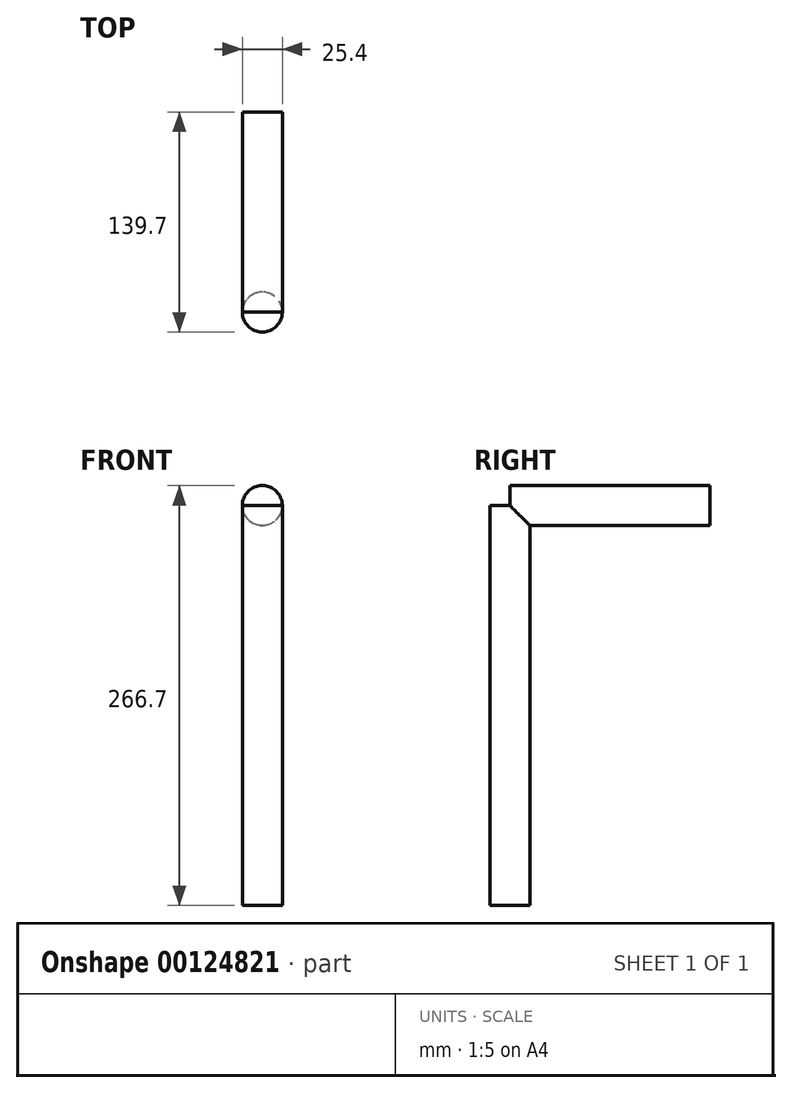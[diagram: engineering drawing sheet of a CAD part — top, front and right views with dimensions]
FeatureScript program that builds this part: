
annotation { "Feature Type Name" : "Feature", "Feature Type Description" : "" }
export const myFeature = defineFeature(function(context is Context, id is Id, definition is map)
    precondition{}
    {
        {
            var Q0;
            Q0=qCreatedBy(makeId("Top.planeOp"),FACE);
            var sketch = newSketch(context, id + "F0", { "sketchPlane" : qUnion([Q0])});
            skCircle(sketch, "E0", {"center": v(0, 0) * mm, "radius": 12.7 * mm});
            skSolve(sketch);
        }
        {
            var Q0;
            Q0=makeQuery(id+"F0.imprint","IMPRINT",FACE,{"disambiguationData":[TD([[makeQuery(id+"F0.imprint","IMPRINT",EDGE,{"derivedFrom":sQuery(id+"F0.wireOp",EDGE,"E0")}),1.0]])]});
            extrude(context, id + "F1", {"entities" : qUnion([Q0]), "oppositeDirection" : true, "depth" : 254 * mm});
        }
        {
            var Q0;
            Q0=qCreatedBy(makeId("Front.planeOp"),FACE);
            var sketch = newSketch(context, id + "F2", { "sketchPlane" : qUnion([Q0])});
            skCircle(sketch, "E1", {"center": v(0, 0) * mm, "radius": 12.7 * mm});
            skSolve(sketch);
        }
        {
            var Q0;
            Q0=makeQuery(id+"F2.imprint","IMPRINT",FACE,{"disambiguationData":[TD([[makeQuery(id+"F2.imprint","IMPRINT",EDGE,{"derivedFrom":sQuery(id+"F2.wireOp",EDGE,"E1")}),1.0]])]});
            extrude(context, id + "F3", {"entities" : qUnion([Q0]), "operationType" : NewBodyOperationType.ADD, "oppositeDirection" : true, "depth" : 127 * mm});
        }
    });
